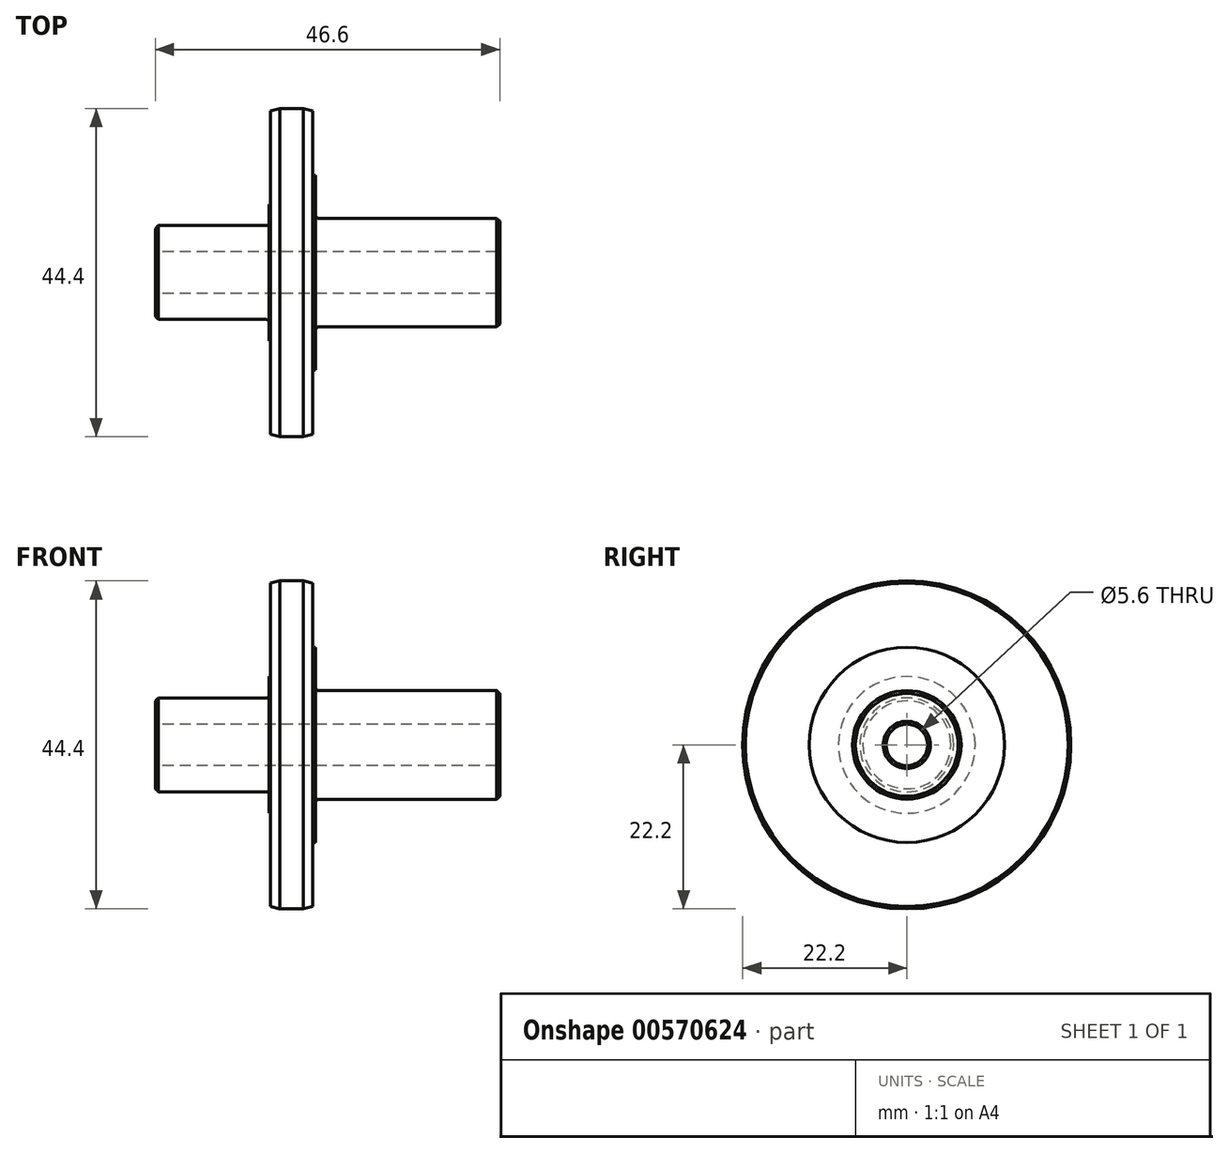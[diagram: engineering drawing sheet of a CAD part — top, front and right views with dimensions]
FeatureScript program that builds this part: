
annotation { "Feature Type Name" : "Feature", "Feature Type Description" : "" }
export const myFeature = defineFeature(function(context is Context, id is Id, definition is map)
    precondition{}
    {
        {
            var Q0;
            Q0=qCreatedBy(makeId("Top.planeOp"),FACE);
            var sketch = newSketch(context, id + "F0", { "sketchPlane" : qUnion([Q0])});
            skLineSegment(sketch, "E0", {"start": v(-12.32, 0) * mm, "end": v(13, 0) * mm, "construction": true});
            skLineSegment(sketch, "E1", {"start": v(-22.87, 2.8) * mm, "end": v(23.73, 2.8) * mm});
            skLineSegment(sketch, "E2", {"start": v(23.73, 2.8) * mm, "end": v(23.73, 7.35) * mm});
            skLineSegment(sketch, "E3", {"start": v(-1.17, 13.2) * mm, "end": v(-1.57, 13.2) * mm});
            skLineSegment(sketch, "E4", {"start": v(-1.57, 13.2) * mm, "end": v(-1.57, 22.2) * mm});
            skLineSegment(sketch, "E5", {"start": v(-1.57, 22.2) * mm, "end": v(-7.27, 22.2) * mm});
            skLineSegment(sketch, "E6", {"start": v(-7.27, 22.2) * mm, "end": v(-7.27, 9.25) * mm});
            skLineSegment(sketch, "E7", {"start": v(-7.27, 9.25) * mm, "end": v(-7.47, 9.25) * mm});
            skLineSegment(sketch, "E8", {"start": v(-7.47, 9.25) * mm, "end": v(-7.47, 6.35) * mm});
            skLineSegment(sketch, "E9", {"start": v(-7.47, 6.35) * mm, "end": v(-22.87, 6.35) * mm});
            skLineSegment(sketch, "E10", {"start": v(-22.87, 6.35) * mm, "end": v(-22.87, 2.8) * mm});
            skLineSegment(sketch, "E11.MirrorCS", {"start": v(-22.87, -2.8) * mm, "end": v(23.73, -2.8) * mm});
            skLineSegment(sketch, "E12.MirrorCS", {"start": v(-22.87, -6.35) * mm, "end": v(-22.87, -2.8) * mm});
            skLineSegment(sketch, "E13.MirrorCS", {"start": v(-7.47, -6.35) * mm, "end": v(-22.87, -6.35) * mm});
            skLineSegment(sketch, "E14", {"start": v(-1.17, 7.35) * mm, "end": v(23.73, 7.35) * mm});
            skLineSegment(sketch, "E15", {"start": v(-1.17, 13.2) * mm, "end": v(-1.17, 7.35) * mm});
            skLineSegment(sketch, "E16.MirrorCS", {"start": v(-7.27, -9.25) * mm, "end": v(-7.47, -9.25) * mm});
            skLineSegment(sketch, "E17.MirrorCS", {"start": v(-1.17, -13.2) * mm, "end": v(-1.57, -13.2) * mm});
            skLineSegment(sketch, "E18.MirrorCS", {"start": v(-7.47, -9.25) * mm, "end": v(-7.47, -6.35) * mm});
            skLineSegment(sketch, "E19.MirrorCS", {"start": v(-1.57, -22.2) * mm, "end": v(-7.27, -22.2) * mm});
            skLineSegment(sketch, "E20.MirrorCS", {"start": v(-1.57, -13.2) * mm, "end": v(-1.57, -22.2) * mm});
            skLineSegment(sketch, "E21.MirrorCS", {"start": v(-1.17, -7.35) * mm, "end": v(23.73, -7.35) * mm});
            skLineSegment(sketch, "E22.MirrorCS", {"start": v(-1.17, -13.2) * mm, "end": v(-1.17, -7.35) * mm});
            skLineSegment(sketch, "E23.MirrorCS", {"start": v(23.73, -2.8) * mm, "end": v(23.73, -7.35) * mm});
            skLineSegment(sketch, "E24.MirrorCS", {"start": v(-7.27, -22.2) * mm, "end": v(-7.27, -9.25) * mm});
            skSolve(sketch);
        }
        {
            var Q0;
            Q0=makeQuery(id+"F0.imprint","IMPRINT",FACE,{"disambiguationData":[TD([[makeQuery(id+"F0.imprint","IMPRINT",EDGE,{"derivedFrom":sQuery(id+"F0.wireOp",EDGE,"E1")}),1.0]])]});
            var Q1;
            Q1=sQuery(id+"F0.wireOp",EDGE,"E0");
            revolve(context, id + "F1", {"entities" : qUnion([Q0]), "axis" : qUnion([Q1]), "revolveType" : RevolveType.FULL});
        }
        {
            var Q0;
            Q0=makeQuery(id+"F1.opRevolve","SWEPT_EDGE",EDGE,{"disambiguationData":[OSD([sQuery(id+"F0.wireOp",EDGE,"E2"),sQuery(id+"F0.wireOp",EDGE,"E14")])]});
            var Q1;
            Q1=makeQuery(id+"F1.opRevolve","SWEPT_EDGE",EDGE,{"disambiguationData":[OSD([sQuery(id+"F0.wireOp",EDGE,"E9"),sQuery(id+"F0.wireOp",EDGE,"E10")])]});
            var Q2;
            Q2=makeQuery(id+"F1.opRevolve","SWEPT_EDGE",EDGE,{"disambiguationData":[OSD([sQuery(id+"F0.wireOp",EDGE,"E1"),sQuery(id+"F0.wireOp",EDGE,"E10")])]});
            var Q3;
            Q3=makeQuery(id+"F1.opRevolve","SWEPT_EDGE",EDGE,{"disambiguationData":[OSD([sQuery(id+"F0.wireOp",EDGE,"E1"),sQuery(id+"F0.wireOp",EDGE,"E2")])]});
            chamfer(context, id + "F2", {"entities" : qUnion([Q0, Q1, Q2, Q3]), "width" : 0.4 * mm, "tangentPropagation" : true});
        }
        {
            var Q0;
            Q0=makeQuery(id+"F1.opRevolve","SWEPT_EDGE",EDGE,{"disambiguationData":[OSD([sQuery(id+"F0.wireOp",EDGE,"E8"),sQuery(id+"F0.wireOp",EDGE,"E9")])]});
            var Q1;
            Q1=makeQuery(id+"F1.opRevolve","SWEPT_EDGE",EDGE,{"disambiguationData":[OSD([sQuery(id+"F0.wireOp",EDGE,"E14"),sQuery(id+"F0.wireOp",EDGE,"E15")])]});
            fillet(context, id + "F3", {"entities" : qUnion([Q0, Q1]), "radius" : .4 * mm, "tangentPropagation" : true, "allowEdgeOverflow" : false});
        }
        {
            var Q0;
            Q0=makeQuery(id+"F1.opRevolve","SWEPT_EDGE",EDGE,{"disambiguationData":[OSD([sQuery(id+"F0.wireOp",EDGE,"E4"),sQuery(id+"F0.wireOp",EDGE,"E5")])]});
            var Q1;
            Q1=makeQuery(id+"F1.opRevolve","SWEPT_EDGE",EDGE,{"disambiguationData":[OSD([sQuery(id+"F0.wireOp",EDGE,"E5"),sQuery(id+"F0.wireOp",EDGE,"E6")])]});
            chamfer(context, id + "F4", {"entities" : qUnion([Q0, Q1]), "chamferType" : ChamferType.OFFSET_ANGLE, "width" : 1.25 * mm, "oppositeDirection" : false, "angle" : 15 * degree, "tangentPropagation" : true});
        }
    });
